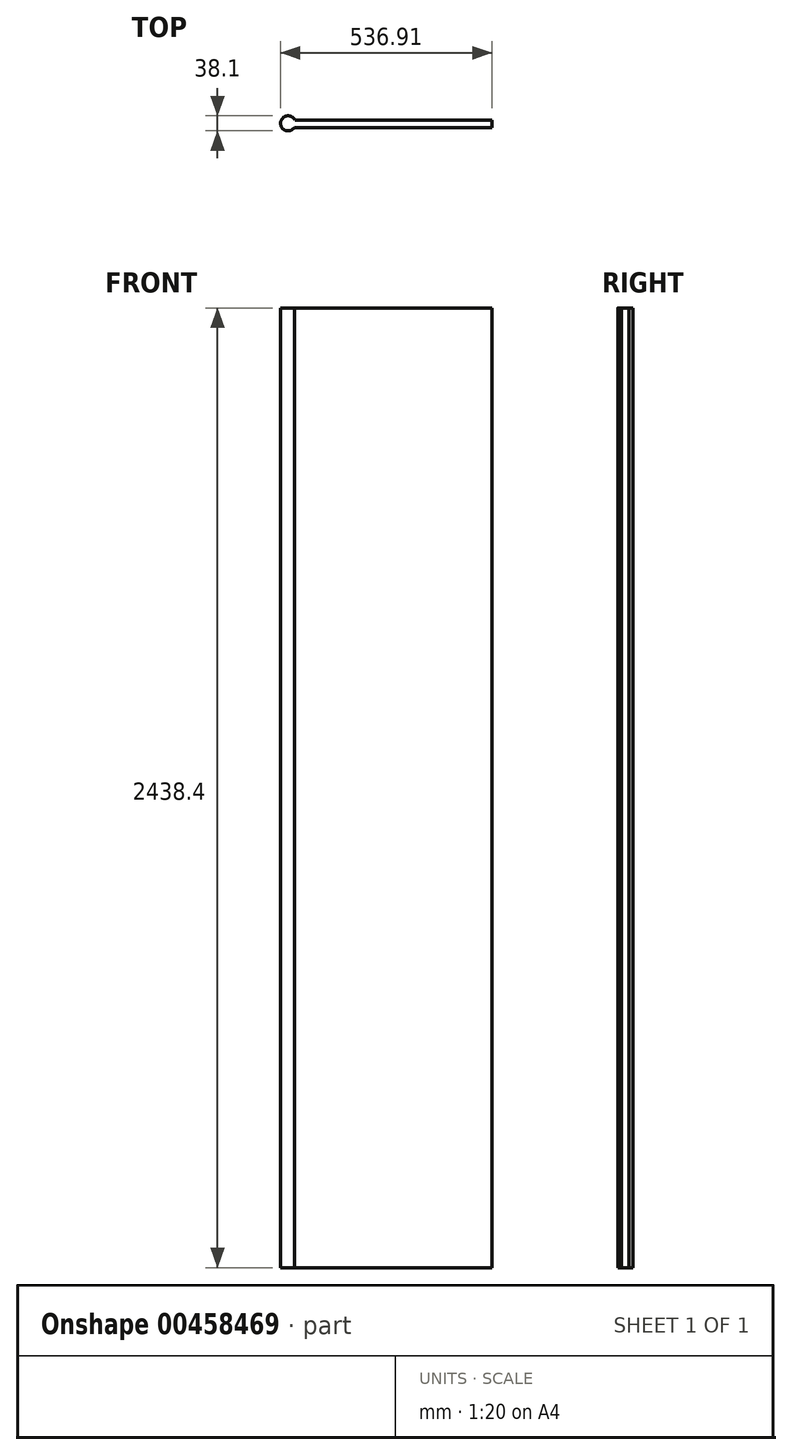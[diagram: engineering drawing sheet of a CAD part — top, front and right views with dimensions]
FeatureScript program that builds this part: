
annotation { "Feature Type Name" : "Feature", "Feature Type Description" : "" }
export const myFeature = defineFeature(function(context is Context, id is Id, definition is map)
    precondition{}
    {
        {
            var Q0;
            Q0=qCreatedBy(makeId("Top.planeOp"),FACE);
            var sketch = newSketch(context, id + "F0", { "sketchPlane" : qUnion([Q0])});
            skLineSegment(sketch, "E0.bottom", {"start": v(-229.16, 25.83) * mm, "end": v(278.84, 25.83) * mm});
            skLineSegment(sketch, "E0.top", {"start": v(-229.16, 6.78) * mm, "end": v(278.84, 6.78) * mm});
            skLineSegment(sketch, "E0.left", {"start": v(-229.16, 25.83) * mm, "end": v(-229.16, 6.78) * mm});
            skLineSegment(sketch, "E0.right", {"start": v(278.84, 25.83) * mm, "end": v(278.84, 6.78) * mm});
            skCircle(sketch, "E1", {"center": v(-239.02, 17.24) * mm, "radius": 19.05 * mm});
            skSolve(sketch);
        }
        {
            var Q0;
            {var subQ0=sQuery(id+"F0.wireOp",EDGE,"E0.left");Q0=makeQuery(id+"F0.imprint","IMPRINT",FACE,{"disambiguationData":[TD([[makeQuery(id+"F0.imprint","IMPRINT",EDGE,{"derivedFrom":subQ0}),-1.0]])]});}
            var Q1;
            {var subQ0=sQuery(id+"F0.wireOp",EDGE,"E0.right");Q1=makeQuery(id+"F0.imprint","IMPRINT",FACE,{"disambiguationData":[TD([[makeQuery(id+"F0.imprint","IMPRINT",EDGE,{"derivedFrom":subQ0}),-1.0]])]});}
            var Q2;
            {var subQ0=sQuery(id+"F0.wireOp",EDGE,"E0.left");Q2=makeQuery(id+"F0.imprint","IMPRINT",FACE,{"disambiguationData":[TD([[makeQuery(id+"F0.imprint","IMPRINT",EDGE,{"derivedFrom":subQ0}),1.0]])]});}
            extrude(context, id + "F1", {"entities" : qUnion([Q0, Q1, Q2]), "endBound" : BoundingType.SYMMETRIC, "depth" : 2438.4 * mm});
        }
    });
